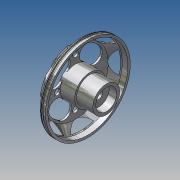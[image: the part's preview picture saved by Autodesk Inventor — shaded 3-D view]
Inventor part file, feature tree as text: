
AUTODESK INVENTOR PART (.ipt)
format: ipt  version: 2015 (Build 190159000, 159)  size: 367,104 bytes
history: native  units: mm
features: sketch x3, extrude x2, revolve x1, fillet x1
ambient origin geometry x8: Origin, YZ Plane, XZ Plane, XY Plane, X Axis, Y Axis, Z Axis, Center Point
bodies: Solid1 (feature_tree)
feature tree (7):
  revolve  "Revolution1"  [1 undecoded]
  fillet  "Fillet1"  Radius=4.0mm
  extrude  "Extrusion1"  Depth=4.5mm
  extrude  "Extrusion2"  Depth=1.0mm
  sketch  "Sketch1"  dims[d2=2.0mm d3=4.0mm d4=4.0mm]
  sketch  "Sketch2"  dims[d5=17.0mm d6=4.5mm]
  sketch  "Sketch3"  dims[d7=5.5mm d8=1.0mm d9=20.9mm d11=3.0mm d12=1.2mm d13=2.9mm d14=18.0mm d15=4.5mm d16=9.0mm d17=7.0mm d18=8.0mm d19=0.7mm d20=1.0mm d21=0.7mm d22=18.24mm d23=90.0deg d24=1.0mm d25=45.0deg d26=5.5mm d27=16.0mm d28=8.0mm d29=40.0mm d31=360.0deg d35=8.0mm d36=80.0mm d38=360.0deg d40=4.0mm d41=0.0mm d42=25.0mm d43=19.0mm d44=3.0mm d45=3.0mm d46=4.0mm d47=0.0mm]
note: 1 required parameter value undecoded (feature->parameter linkage not recoverable at this tier; creation-order binding heuristic only, values carry confidence <= 0.55)
